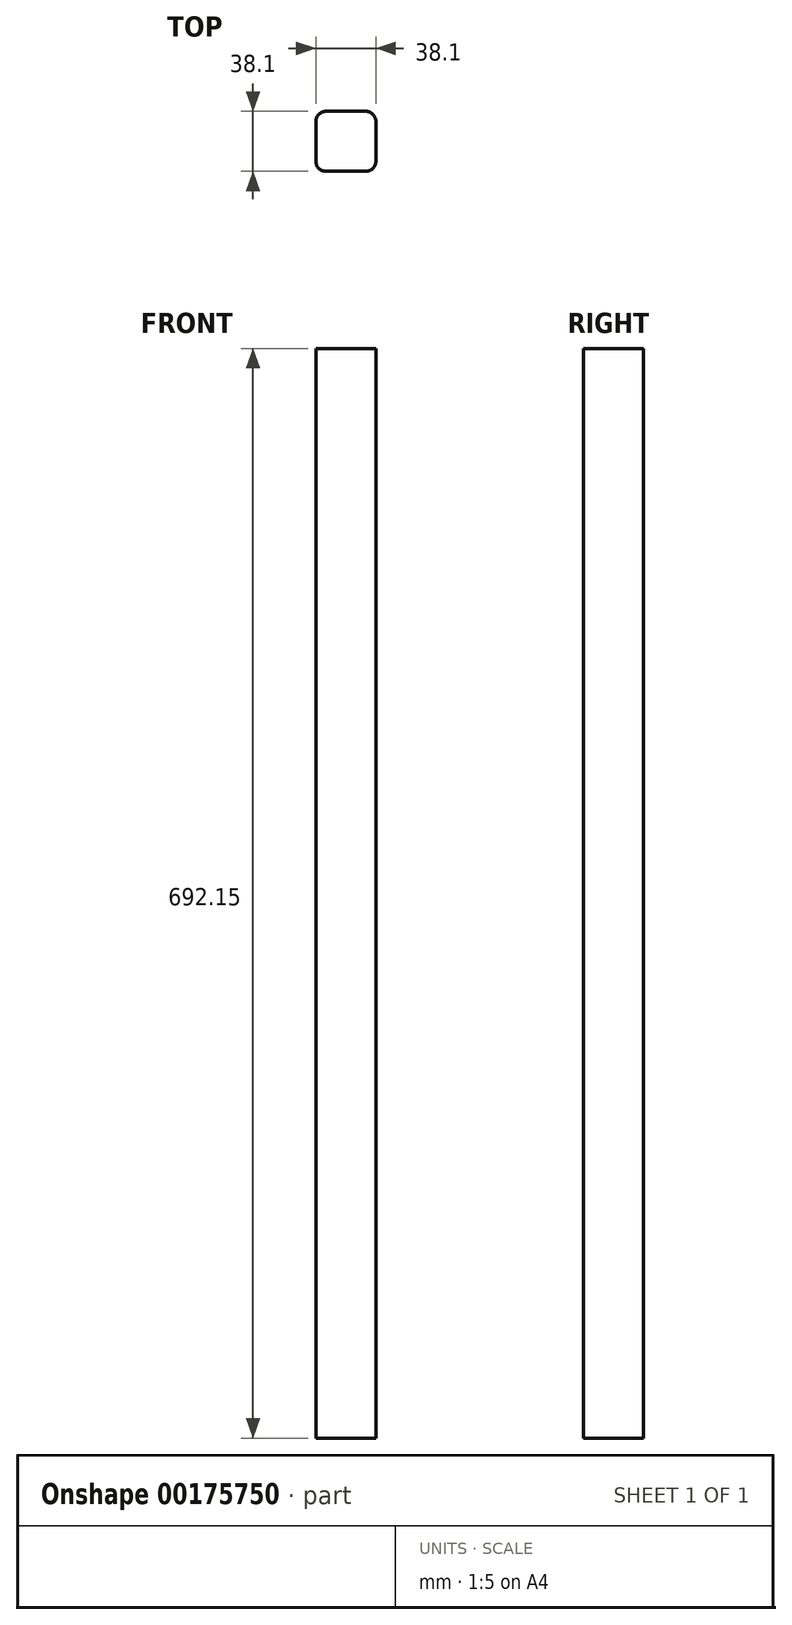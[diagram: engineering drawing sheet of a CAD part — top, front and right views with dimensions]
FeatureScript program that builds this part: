
annotation { "Feature Type Name" : "Feature", "Feature Type Description" : "" }
export const myFeature = defineFeature(function(context is Context, id is Id, definition is map)
    precondition{}
    {
        {
            var Q0;
            Q0=qCreatedBy(makeId("Top.planeOp"),FACE);
            var sketch = newSketch(context, id + "F0", { "sketchPlane" : qUnion([Q0])});
            skLineSegment(sketch, "E0.bottom", {"start": v(12.7, 19.05) * mm, "end": v(-12.7, 19.05) * mm});
            skLineSegment(sketch, "E0.top", {"start": v(12.7, -19.05) * mm, "end": v(-12.7, -19.05) * mm});
            skLineSegment(sketch, "E0.left", {"start": v(19.05, 12.7) * mm, "end": v(19.05, -12.7) * mm});
            skLineSegment(sketch, "E0.right", {"start": v(-19.05, 12.7) * mm, "end": v(-19.05, -12.7) * mm});
            skPoint(sketch, "E0.middle", {"position": v(0, 0) * mm});
            skPoint(sketch, "E1.visualSharp", {"position": v(19.05, 19.05) * mm});
            skArc(sketch, "E1.filletArc", {"start": v(19.05, 12.7) * mm, "mid": v(17.2, 17.2) * mm, "end": v(12.7, 19.05) * mm});
            skPoint(sketch, "E2.visualSharp", {"position": v(-19.05, 19.05) * mm});
            skArc(sketch, "E2.filletArc", {"start": v(-12.7, 19.05) * mm, "mid": v(-17.2, 17.2) * mm, "end": v(-19.05, 12.7) * mm});
            skPoint(sketch, "E3.visualSharp", {"position": v(-19.05, -19.05) * mm});
            skArc(sketch, "E3.filletArc", {"start": v(-19.05, -12.7) * mm, "mid": v(-17.2, -17.2) * mm, "end": v(-12.7, -19.05) * mm});
            skPoint(sketch, "E4.visualSharp", {"position": v(19.05, -19.05) * mm});
            skArc(sketch, "E4.filletArc", {"start": v(12.7, -19.05) * mm, "mid": v(17.2, -17.2) * mm, "end": v(19.05, -12.7) * mm});
            skSolve(sketch);
        }
        {
            var Q0;
            Q0=qSketchRegion(id+"F0",true);
            extrude(context, id + "F1", {"entities" : qUnion([Q0]), "depth" : 692.15 * mm});
        }
    });
